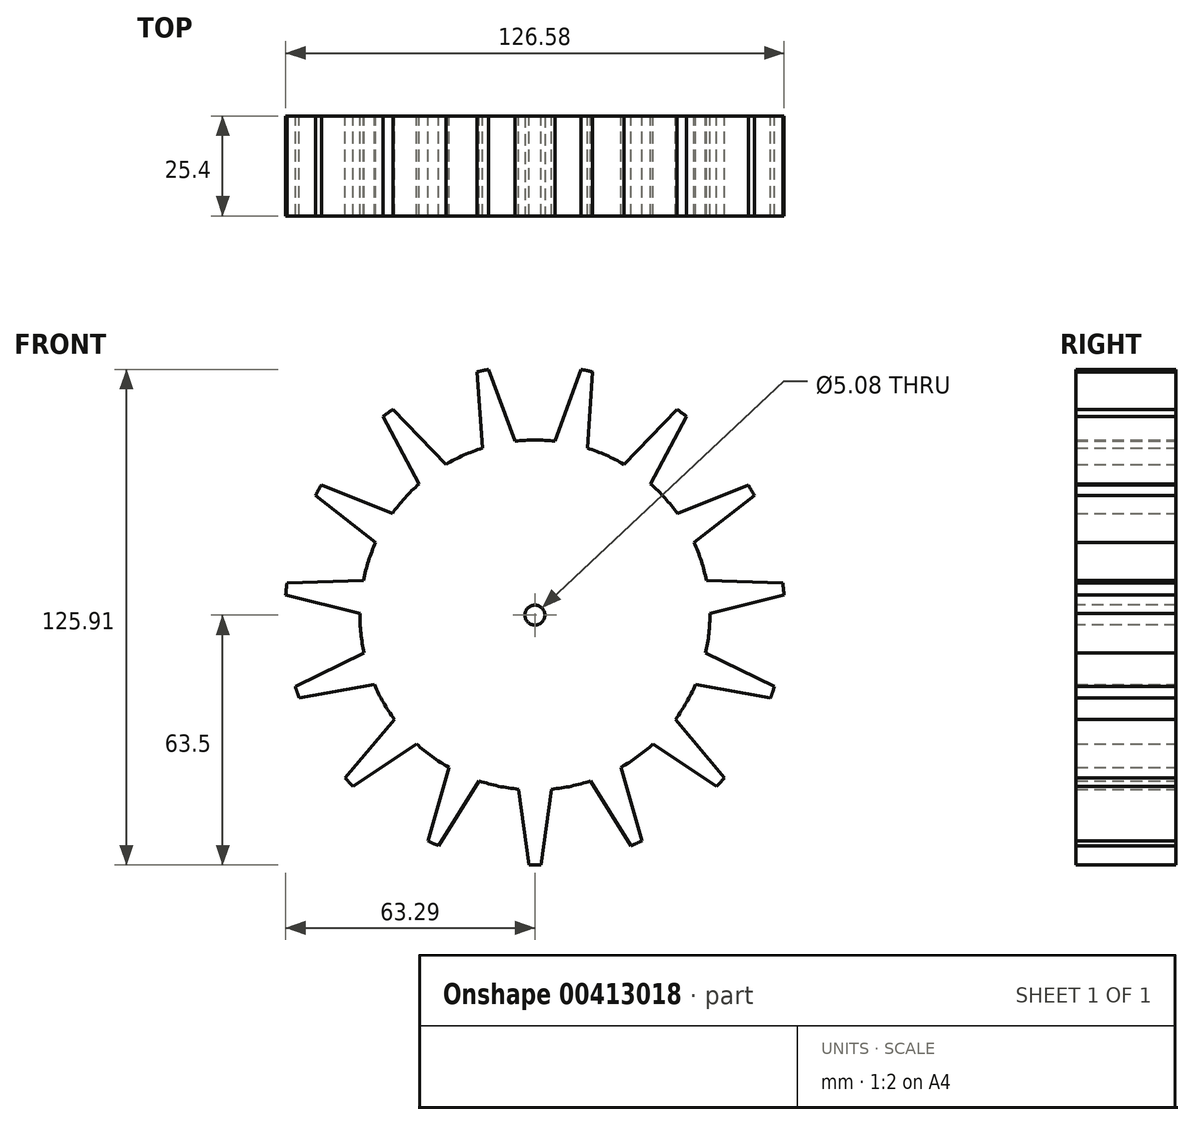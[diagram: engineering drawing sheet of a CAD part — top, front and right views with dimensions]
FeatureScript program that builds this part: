
annotation { "Feature Type Name" : "Feature", "Feature Type Description" : "" }
export const myFeature = defineFeature(function(context is Context, id is Id, definition is map)
    precondition{}
    {
        {
            var Q0;
            Q0=qCreatedBy(makeId("Front.planeOp"),FACE);
            var sketch = newSketch(context, id + "F0", { "sketchPlane" : qUnion([Q0])});
            skCircle(sketch, "E0", {"center": v(0, 0) * mm, "radius": 63.5 * mm});
            skCircle(sketch, "E1", {"center": v(0, 0) * mm, "radius": 44.45 * mm});
            skLineSegment(sketch, "E2", {"start": v(0, 0) * mm, "end": v(0, 63.5) * mm, "construction": true});
            skLineSegment(sketch, "E3", {"start": v(5.08, 44.16) * mm, "end": v(11.72, 62.4) * mm});
            skLineSegment(sketch, "E4.MirrorCS", {"start": v(-5.08, 44.16) * mm, "end": v(-11.72, 62.4) * mm});
            skSolve(sketch);
        }
        {
            var Q0;
            {var subQ0=sQuery(id+"F0.wireOp",EDGE,"E1");var subQ1=makeQuery(id+"F0.imprint","INTERSECT",VERTEX,{"derivedFrom":[subQ0,sQuery(id+"F0.wireOp",EDGE,"E3")]});Q0=makeQuery(id+"F0.imprint","IMPRINT",FACE,{"disambiguationData":[TD([[makeQuery(id+"F0.imprint","IMPRINT",EDGE,{"disambiguationData":[TD([[subQ1,-1.0]])],"derivedFrom":subQ0}),1.0]])]});}
            var Q1;
            {var subQ0=sQuery(id+"F0.wireOp",EDGE,"E3");Q1=makeQuery(id+"F0.imprint","IMPRINT",FACE,{"disambiguationData":[TD([[makeQuery(id+"F0.imprint","IMPRINT",EDGE,{"derivedFrom":subQ0}),-1.0]])]});}
            extrude(context, id + "F1", {"entities" : qUnion([Q0, Q1]), "depth" : 25.4 * mm});
        }
        {
            var Q0;
            Q0=makeQuery(id+"F1.opExtrude","SWEPT_FACE",FACE,{"disambiguationData":[OSD([sQuery(id+"F0.wireOp",EDGE,"E4.MirrorCS")])]});
            var Q1;
            Q1=makeQuery(id+"F1.opExtrude","SWEPT_FACE",FACE,{"disambiguationData":[OSD([sQuery(id+"F0.wireOp",EDGE,"E1")])]});
            var Q2;
            Q2=makeQuery(id+"F1.opExtrude","SWEPT_FACE",FACE,{"disambiguationData":[OSD([sQuery(id+"F0.wireOp",EDGE,"E3")])]});
            var Q3;
            Q3=makeQuery(id+"F1.opExtrude","SWEPT_FACE",FACE,{"disambiguationData":[OSD([sQuery(id+"F0.wireOp",EDGE,"E0")])]});
            circularPattern(context, id + "F2", {"patternType" : PatternType.FACE, "faces" : qUnion([Q0, Q1, Q2]), "axis" : qUnion([Q3]), "angle" : 360 * degree, "instanceCount" : 30, "equalSpace" : true});
        }
        {
            var Q0;
            Q0=makeQuery(id+"F1.opExtrude","CAP_FACE",FACE,{"disambiguationData":[OSD([sQuery(id+"F0.wireOp",EDGE,"E0"),sQuery(id+"F0.wireOp",EDGE,"E1"),sQuery(id+"F0.wireOp",EDGE,"E3"),sQuery(id+"F0.wireOp",EDGE,"E4.MirrorCS")])],"isStart":false});
            var sketch = newSketch(context, id + "F3", { "sketchPlane" : qUnion([Q0])});
            skPoint(sketch, "E5", {"position": v(0, 0) * mm});
            skSolve(sketch);
        }
        {
            var Q0;
            Q0=sQuery(id+"F3.wireOp",VERTEX,"E5");
            var Q1;
            Q1=makeQuery(id+"F1.opExtrude","SWEPT_BODY",BODY,{"disambiguationData":[OSD([sQuery(id+"F0.wireOp",EDGE,"E0"),sQuery(id+"F0.wireOp",EDGE,"E1"),sQuery(id+"F0.wireOp",EDGE,"E3"),sQuery(id+"F0.wireOp",EDGE,"E4.MirrorCS")])]});
            hole(context, id + "F4", {"style" : HoleStyle.SIMPLE, "endStyle" : HoleEndStyle.THROUGH, "holeDiameter" : 5.08 * mm, "isTappedThrough" : true, "tappedDepth" : 12.7 * mm, "tapClearance" : 3, "locations" : qUnion([Q0]), "scope" : qUnion([Q1])});
        }
    });
